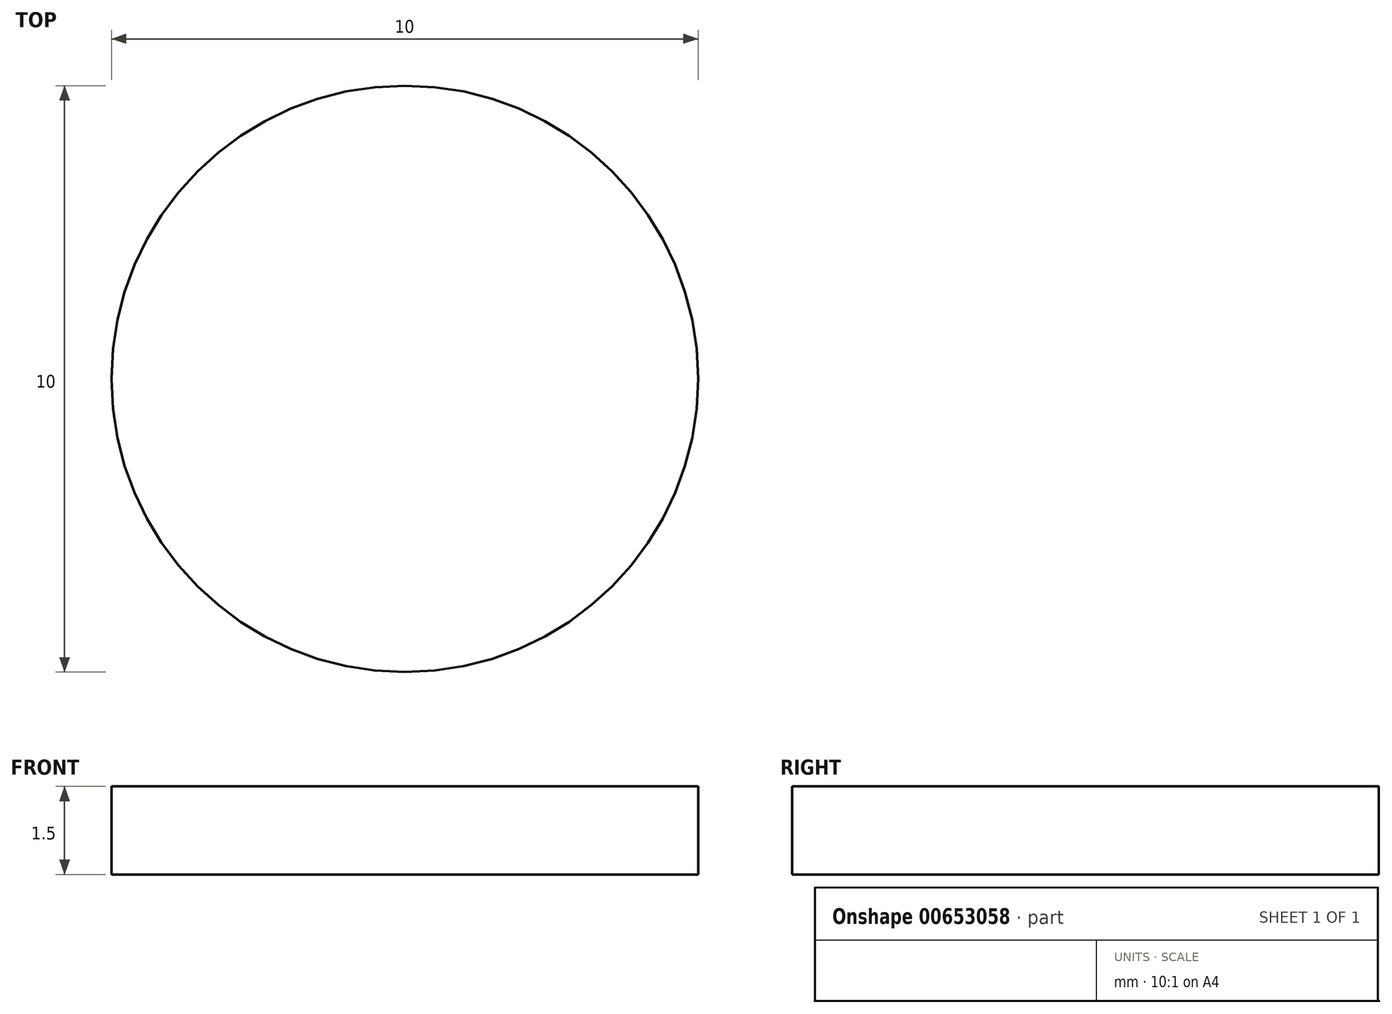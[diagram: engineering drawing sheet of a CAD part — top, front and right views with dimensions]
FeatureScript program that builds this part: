
annotation { "Feature Type Name" : "Feature", "Feature Type Description" : "" }
export const myFeature = defineFeature(function(context is Context, id is Id, definition is map)
    precondition{}
    {
        {
            var Q0;
            Q0=qCreatedBy(makeId("Top.planeOp"),FACE);
            var sketch = newSketch(context, id + "F0", { "sketchPlane" : qUnion([Q0])});
            skCircle(sketch, "E0", {"center": v(0, 0) * mm, "radius": 5 * mm});
            skSolve(sketch);
        }
        {
            var Q0;
            Q0=makeQuery(id+"F0.imprint","IMPRINT",FACE,{"disambiguationData":[TD([[makeQuery(id+"F0.imprint","IMPRINT",EDGE,{"derivedFrom":sQuery(id+"F0.wireOp",EDGE,"E0")}),1.0]])]});
            extrude(context, id + "F1", {"entities" : qUnion([Q0]), "depth" : 1.5 * mm, "offsetDistance" : 25 * mm});
        }
    });
